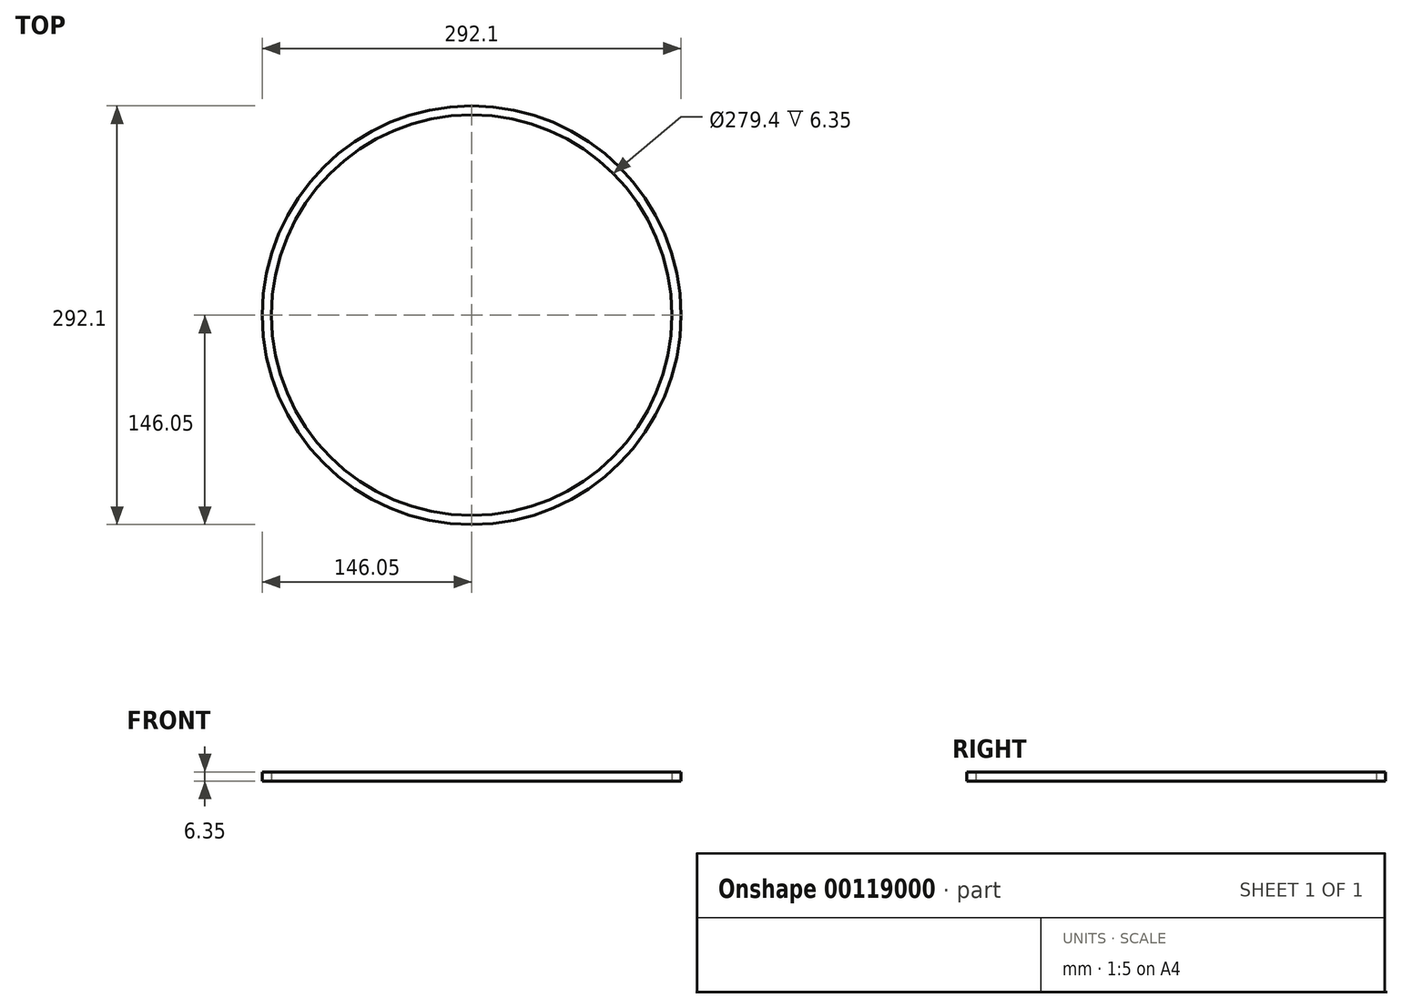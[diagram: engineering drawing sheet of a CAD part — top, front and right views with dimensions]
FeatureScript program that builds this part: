
annotation { "Feature Type Name" : "Feature", "Feature Type Description" : "" }
export const myFeature = defineFeature(function(context is Context, id is Id, definition is map)
    precondition{}
    {
        {
            var Q0;
            Q0=qCreatedBy(makeId("Top.planeOp"),FACE);
            var sketch = newSketch(context, id + "F0", { "sketchPlane" : qUnion([Q0])});
            skCircle(sketch, "E0", {"center": v(0, 0) * mm, "radius": 139.7 * mm});
            skCircle(sketch, "E1", {"center": v(0, 0) * mm, "radius": 146.05 * mm});
            skSolve(sketch);
        }
        {
            var Q0;
            Q0=makeQuery(id+"F0.imprint","IMPRINT",FACE,{"disambiguationData":[TD([[makeQuery(id+"F0.imprint","IMPRINT",EDGE,{"derivedFrom":sQuery(id+"F0.wireOp",EDGE,"E0")}),-1.0]])]});
            var Q1;
            Q1=sQuery(id+"F0.wireOp",EDGE,"E0");
            var Q2;
            Q2=sQuery(id+"F0.wireOp",EDGE,"E1");
            extrude(context, id + "F1", {"entities" : qUnion([Q0]), "surfaceEntities" : qUnion([Q1, Q2]), "depth" : 6.35 * mm});
        }
    });
